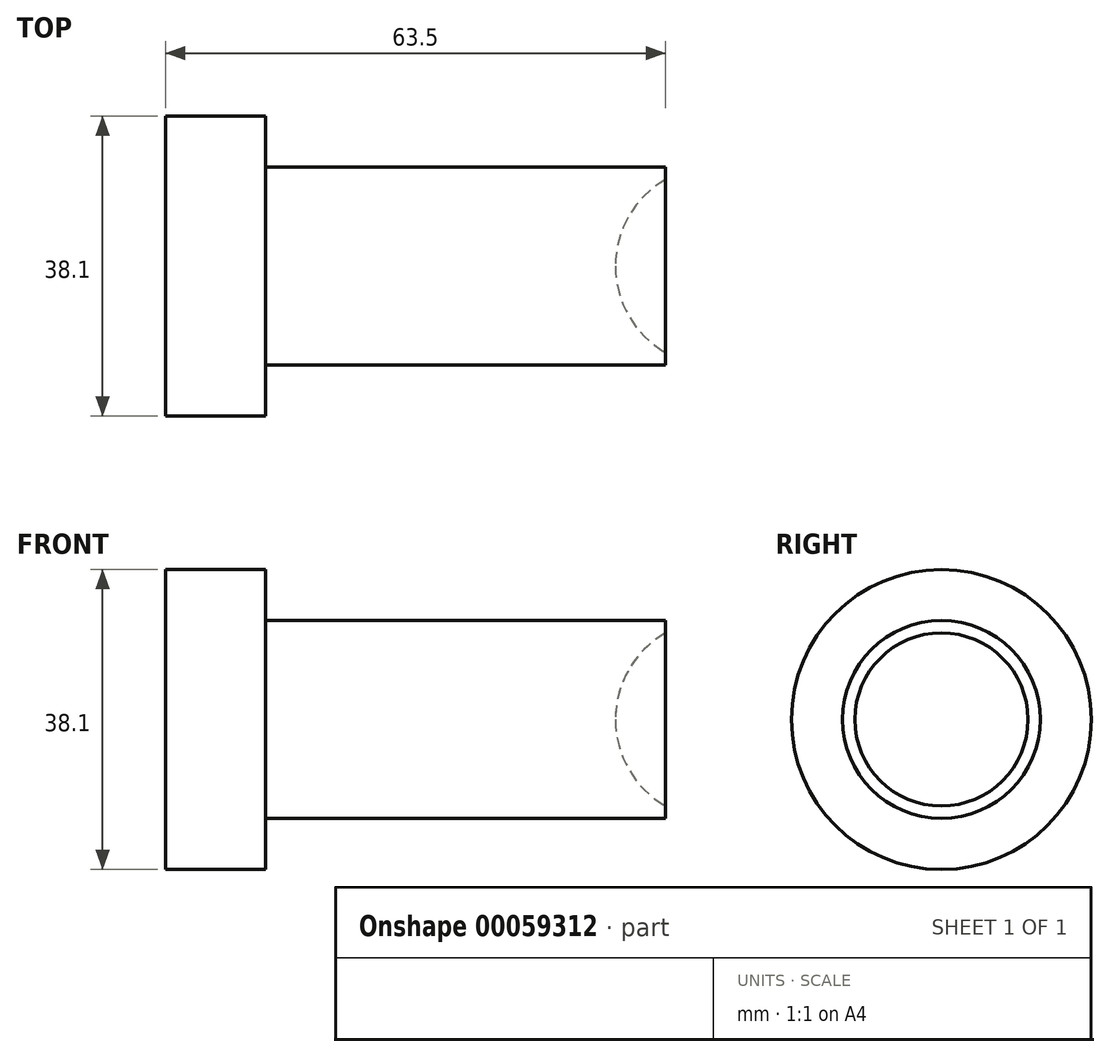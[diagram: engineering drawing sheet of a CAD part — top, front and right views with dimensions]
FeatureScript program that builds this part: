
annotation { "Feature Type Name" : "Feature", "Feature Type Description" : "" }
export const myFeature = defineFeature(function(context is Context, id is Id, definition is map)
    precondition{}
    {
        {
            var Q0;
            Q0=qCreatedBy(makeId("Front.planeOp"),FACE);
            var sketch = newSketch(context, id + "F0", { "sketchPlane" : qUnion([Q0])});
            skLineSegment(sketch, "E0", {"start": v(-12.7, 19.05) * mm, "end": v(-12.7, 0) * mm});
            skLineSegment(sketch, "E1", {"start": v(-12.7, 0) * mm, "end": v(44.45, 0) * mm});
            skLineSegment(sketch, "E2", {"start": v(50.8, 11) * mm, "end": v(50.8, 12.57) * mm});
            skLineSegment(sketch, "E3", {"start": v(50.8, 12.57) * mm, "end": v(0, 12.57) * mm});
            skLineSegment(sketch, "E4", {"start": v(0, 12.57) * mm, "end": v(0, 19.05) * mm});
            skLineSegment(sketch, "E5", {"start": v(0, 19.05) * mm, "end": v(-12.7, 19.05) * mm});
            skLineSegment(sketch, "E6", {"start": v(0, 12.57) * mm, "end": v(0, 0) * mm});
            skArc(sketch, "E7", {"start": v(50.8, 11) * mm, "mid": v(46.15, 6.35) * mm, "end": v(44.45, 0) * mm});
            skPoint(sketch, "E8.orphan", {"position": v(50.8, 0) * mm});
            skSolve(sketch);
        }
        {
            var Q0;
            Q0 = qSketchRegion(id + "F0", true);
            var Q1;
            Q1=sQuery(id+"F0.wireOp",EDGE,"E1");
            revolve(context, id + "F1", {"entities" : qUnion([Q0]), "axis" : qUnion([Q1]), "revolveType" : RevolveType.FULL});
        }
    });
